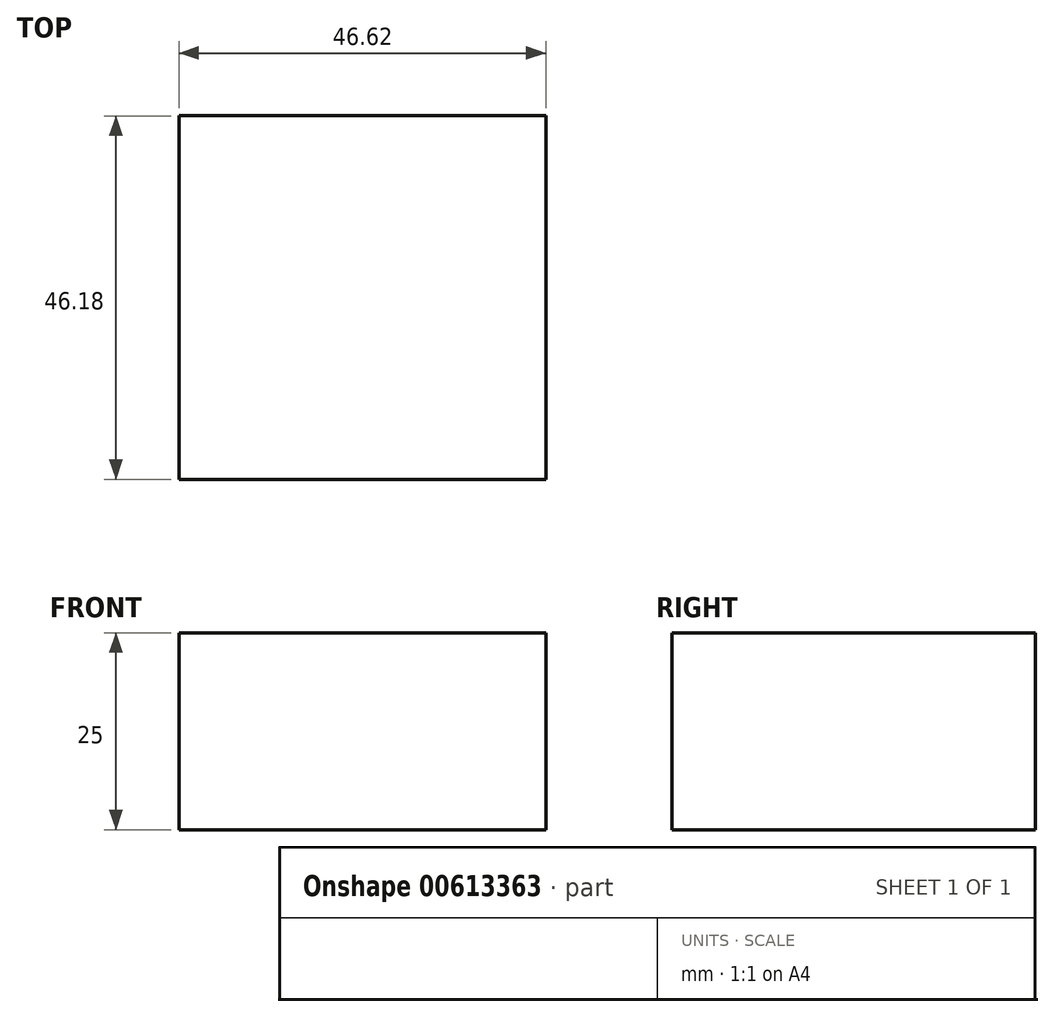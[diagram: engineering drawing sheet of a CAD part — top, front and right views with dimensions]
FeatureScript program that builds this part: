
annotation { "Feature Type Name" : "Feature", "Feature Type Description" : "" }
export const myFeature = defineFeature(function(context is Context, id is Id, definition is map)
    precondition{}
    {
        {
            var Q0;
            Q0=qCreatedBy(makeId("Top.planeOp"),FACE);
            var sketch = newSketch(context, id + "F0", { "sketchPlane" : qUnion([Q0])});
            skLineSegment(sketch, "E0.bottom", {"start": v(-18.2, 23.04) * mm, "end": v(28.42, 23.04) * mm});
            skLineSegment(sketch, "E0.top", {"start": v(-18.2, -23.14) * mm, "end": v(28.42, -23.14) * mm});
            skLineSegment(sketch, "E0.left", {"start": v(-18.2, 23.04) * mm, "end": v(-18.2, -23.14) * mm});
            skLineSegment(sketch, "E0.right", {"start": v(28.42, 23.04) * mm, "end": v(28.42, -23.14) * mm});
            skSolve(sketch);
        }
        {
            var Q0;
            Q0=makeQuery(id+"F0.imprint","IMPRINT",FACE,{"disambiguationData":[TD([[makeQuery(id+"F0.imprint","IMPRINT",EDGE,{"derivedFrom":sQuery(id+"F0.wireOp",EDGE,"E0.bottom")}),-1.0]])]});
            extrude(context, id + "F1", {"entities" : qUnion([Q0]), "depth" : 25 * mm, "offsetDistance" : 25 * mm});
        }
    });
